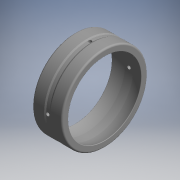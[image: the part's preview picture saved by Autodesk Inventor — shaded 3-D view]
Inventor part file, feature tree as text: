
AUTODESK INVENTOR PART (.ipt)
format: ipt  version: 2017.3 (Build 213256000, 256)  size: 199,168 bytes
history: native  units: mm (DEFAULTED — no unit token found)
features: other x14, revolve x4, sketch x4
ambient origin geometry x8: Origin, YZ Plane, XZ Plane, XY Plane, X Axis, Y Axis, Z Axis, Center Point
bodies: Solid1 (feature_tree)
feature tree (22):
  revolve  "Revolution1"  Angle=360.0deg
  revolve  "Revolution2"  Angle=360.0deg
  revolve  "Revolution3"  [1 undecoded]
  revolve  "Revolution4"  [1 undecoded]
  other  "NO_GEO_XY"
  other  "NO_GEO_YZ"
  other  "NO_GEO_ZX"
  other  "NO_GEO_X"
  other  "NO_GEO_Y"
  other  "NO_GEO_Z"
  other  "NO_GEO_Center"
  other  "or_XY"
  other  "or_YZ"
  other  "or_ZX"
  other  "or_X"
  other  "or_Y"
  other  "or_Z"
  other  "or_Center"
  sketch  "Sketch_5"  dims[d2=360.0deg d3=360.0deg]
  sketch  "Sketch_2"  dims[d0=360.0deg d1=360.0deg]
  sketch  "Sketch_9"  dims[d4=0.0mm]
  sketch  "Sketch_10"
note: 2 required parameter values undecoded (feature->parameter linkage not recoverable at this tier; creation-order binding heuristic only, values carry confidence <= 0.55)
